MODEL slx_21d225949edd
KIND model
CONFIG InitFcn = clear functions
BLOCK [Clock] Clock
BLOCK [TransferFcn] DC Servo 1
  Denominator = [1 1 0]
  Numerator = [1000]
BLOCK [TransferFcn] DC Servo 2
  Denominator = [1 1 0]
  Numerator = [1000]
BLOCK [TransferFcn] DC Servo 3
  Denominator = [1 1 0]
  Numerator = [1000]
BLOCK [Demux] Demux
  Outputs = 3
  Ports = [1, 3]
BLOCK [Display] Display
  Decimation = 1
  Lockdown = off
  Ports = [1]
BLOCK [Mux] Mux
  DisplayOption = bar
  Ports = [4, 1]
BLOCK [Mux] Mux1
  DisplayOption = bar
  Inputs = 2
  Ports = [2, 1]
BLOCK [Mux] Mux2
  DisplayOption = bar
  Inputs = 2
  Ports = [2, 1]
BLOCK [Mux] Mux3
  DisplayOption = bar
  Inputs = 2
  Ports = [2, 1]
BLOCK [Scope] Schedule
  DataFormat = StructureWithTime
  Floating = off
  LimitDataPoints = off
  NumInputPorts = 1
  Ports = [1]
  SaveName = ry
  SaveToWorkspace = on
  ShowLegends = off
  TimeRange = 1
  YMax = 3.5
  YMin = 1
  ZoomMode = xonly
BLOCK [SignalGenerator] Signal Generator
  Frequency = 1.5
  Ports = [0, 1]
  WaveForm = square
BLOCK [Reference] TrueTime Kernel  REF=truetime/TrueTime Kernel  (lib defined in slx_0362a698a4ec)
  Ports = [1, 2]
  SourceBlock = truetime/TrueTime Kernel
  UserDataPersistent = on
  args = 1
  battery = off
  clockoffsetdrift = [0 0]
  ninputsoutputs = [4 3]
  ntriggers = 0
  nwnodenbr = []
  poweroutput = off
  schedoutput = on
  sfun = threeservos_init
  trigtype = falling
BLOCK [Scope] r,y
  DataFormat = StructureWithTime
  Floating = off
  LimitDataPoints = off
  NumInputPorts = 3
  Ports = [3]
  SaveName = ry1
  SaveToWorkspace = on
  ShowLegends = off
  TimeRange = 1
  YMax = 2~2~2
  YMin = -2~-2~-2
BLOCK [Scope] u
  DataFormat = StructureWithTime
  Floating = off
  LimitDataPoints = off
  NumInputPorts = 3
  Ports = [3]
  ShowLegends = off
  TimeRange = 1
  YMax = 2~5~5
  YMin = -2~-5~-5
ANNOTATION (root): The TrueTime Kernel init function argument determines the scheduling policy used: 1: Deadline-monotonic (DM) scheduling 2: Earliest-deadline-first (EDF) scheduling 3: EDF scheduling with deadline overrun handler that kills all jobs that miss their deadlines 4: EDF scheduling with job skips - a task that finishes late skips the next job 5: EDF scheduling with controller 3 executing inside a constan...<+108ch>
ANNOTATION (root): TrueTime 2.0 Task Scheduling and Control <copyright redacted>
LINE Clock:1 -> Display:1
NET DC Servo 1:1 -> Mux3:2, Mux:2
NET DC Servo 2:1 -> Mux1:2, Mux:3
NET DC Servo 3:1 -> Mux2:2, Mux:4
NET Demux:1 -> DC Servo 1:1, u:1
NET Demux:2 -> DC Servo 2:1, u:2
NET Demux:3 -> DC Servo 3:1, u:3
LINE Mux1:1 -> r,y:2
LINE Mux2:1 -> r,y:3
LINE Mux3:1 -> r,y:1
LINE Mux:1 -> TrueTime Kernel:1
NET Signal Generator:1 -> Mux1:1, Mux2:1, Mux3:1, Mux:1
LINE TrueTime Kernel:1 -> Demux:1
LINE TrueTime Kernel:2 -> Schedule:1
note: NET lines group one-source signal fan-out (src -> all destinations, sorted); 1:1 wires keep LINE
